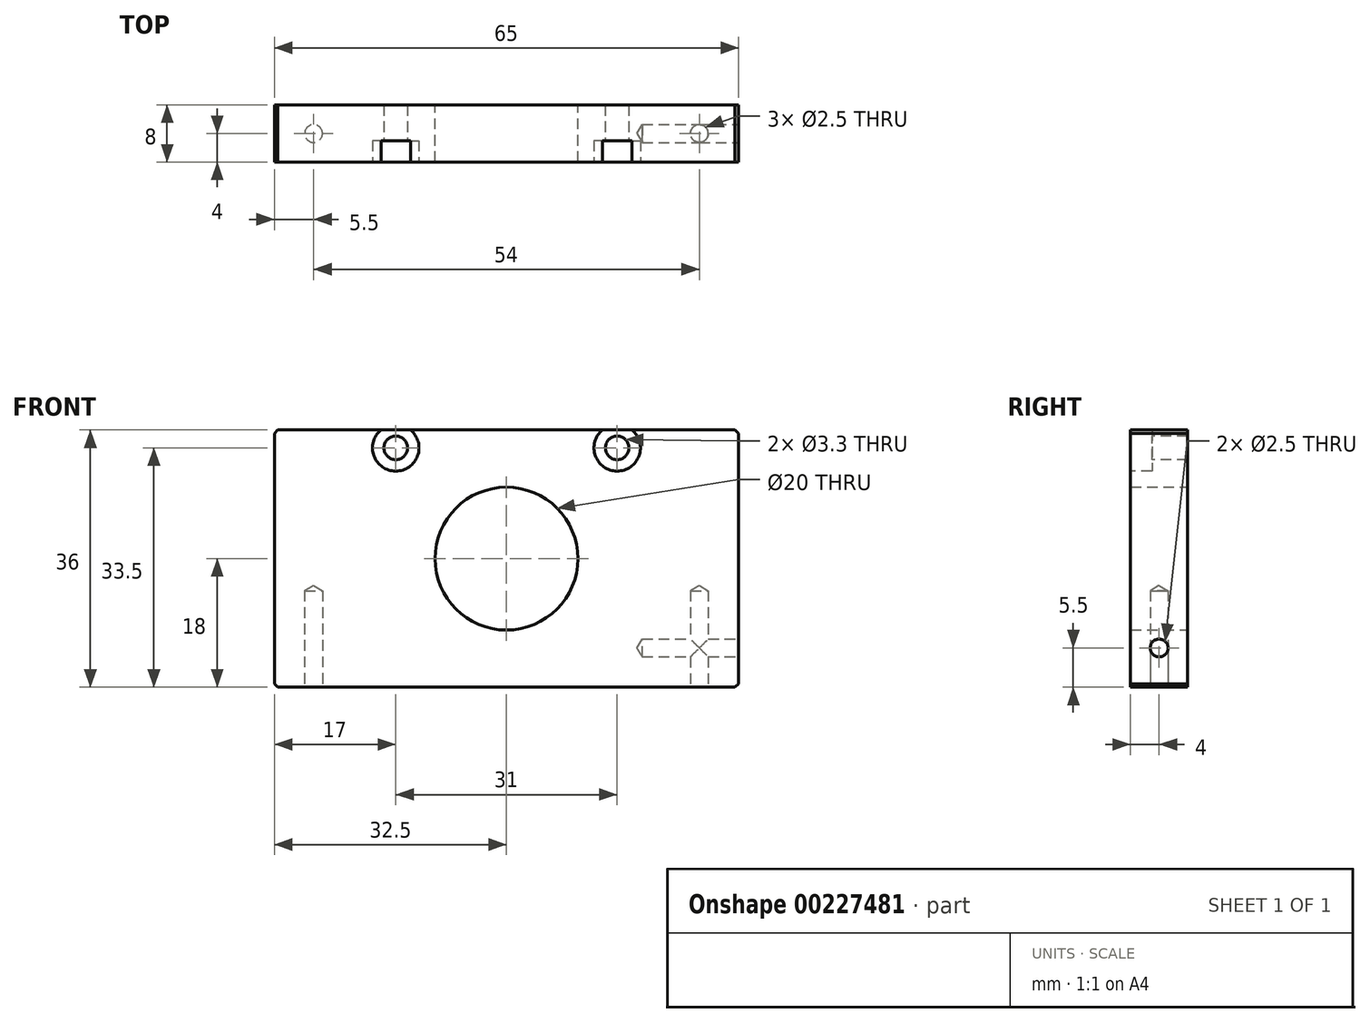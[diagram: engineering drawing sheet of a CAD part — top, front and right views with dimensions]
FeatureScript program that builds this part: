
annotation { "Feature Type Name" : "Feature", "Feature Type Description" : "" }
export const myFeature = defineFeature(function(context is Context, id is Id, definition is map)
    precondition{}
    {
        {
            var Q0;
            Q0=qCreatedBy(makeId("Front.planeOp"),FACE);
            var sketch = newSketch(context, id + "F0", { "sketchPlane" : qUnion([Q0])});
            skLineSegment(sketch, "E0.bottom", {"start": v(32.5, -18) * mm, "end": v(-32.5, -18) * mm});
            skLineSegment(sketch, "E0.top", {"start": v(32.5, 18) * mm, "end": v(-32.5, 18) * mm});
            skLineSegment(sketch, "E0.left", {"start": v(32.5, -18) * mm, "end": v(32.5, 18) * mm});
            skLineSegment(sketch, "E0.right", {"start": v(-32.5, -18) * mm, "end": v(-32.5, 18) * mm});
            skPoint(sketch, "E0.middle", {"position": v(0, 0) * mm});
            skCircle(sketch, "E1", {"center": v(0, 0) * mm, "radius": 10 * mm});
            skSolve(sketch);
        }
        {
            var Q0;
            Q0=makeQuery(id+"F0.imprint","IMPRINT",FACE,{"disambiguationData":[TD([[makeQuery(id+"F0.imprint","IMPRINT",EDGE,{"derivedFrom":sQuery(id+"F0.wireOp",EDGE,"E0.bottom")}),-1.0]])]});
            extrude(context, id + "F1", {"entities" : qUnion([Q0]), "depth" : 8 * mm});
        }
        {
            var Q0;
            Q0=makeQuery(id+"F1.opExtrude","CAP_FACE",FACE,{"disambiguationData":[OSD([sQuery(id+"F0.wireOp",EDGE,"E0.bottom"),sQuery(id+"F0.wireOp",EDGE,"E0.top"),sQuery(id+"F0.wireOp",EDGE,"E0.left"),sQuery(id+"F0.wireOp",EDGE,"E0.right")])],"isStart":false});
            var sketch = newSketch(context, id + "F2", { "sketchPlane" : qUnion([Q0])});
            skPoint(sketch, "E2", {"position": v(15.5, 15.5) * mm});
            skPoint(sketch, "E3.MirrorP", {"position": v(-15.5, 15.5) * mm});
            skPoint(sketch, "E4.MirrorP", {"position": v(15.5, -15.5) * mm});
            skPoint(sketch, "E5.MirrorP", {"position": v(-15.5, -15.5) * mm});
            skSolve(sketch);
        }
        {
            var Q0;
            Q0=sQuery(id+"F2.wireOp",VERTEX,"E2");
            var Q1;
            Q1=sQuery(id+"F2.wireOp",VERTEX,"E3.MirrorP");
            var Q2;
            Q2=makeQuery(id+"F1.opExtrude","SWEPT_BODY",BODY,{"disambiguationData":[OSD([sQuery(id+"F0.wireOp",EDGE,"E0.bottom"),sQuery(id+"F0.wireOp",EDGE,"E0.top"),sQuery(id+"F0.wireOp",EDGE,"E0.left"),sQuery(id+"F0.wireOp",EDGE,"E0.right")])]});
            hole(context, id + "F3", {"style" : HoleStyle.C_BORE, "endStyle" : HoleEndStyle.THROUGH, "standardTappedOrClearance" : lookupTablePath({ "standard" : "ISO", "fit" : "Normal", "size" : "M3", "type" : "Clearance" }), "standardBlindInLast" : lookupTablePath({ "fit" : "Standard", "standard" : "ISO", "size" : "M3", "type" : "Clearance" }), "holeDiameter" : 3.3 * mm, "cBoreDiameter" : 6.5 * mm, "cBoreDepth" : 3 * mm, "locations" : qUnion([Q0, Q1]), "scope" : qUnion([Q2]), "tappedDepth" : 12 * mm, "tapClearance" : 3});
        }
        {
            var Q0;
            Q0=makeQuery(id+"F1.opExtrude","SWEPT_EDGE",EDGE,{"disambiguationData":[OSD([sQuery(id+"F0.wireOp",EDGE,"E0.top"),sQuery(id+"F0.wireOp",EDGE,"E0.right")])]});
            var Q1;
            Q1=makeQuery(id+"F1.opExtrude","SWEPT_EDGE",EDGE,{"disambiguationData":[OSD([sQuery(id+"F0.wireOp",EDGE,"E0.top"),sQuery(id+"F0.wireOp",EDGE,"E0.left")])]});
            var Q2;
            Q2=makeQuery(id+"F1.opExtrude","SWEPT_EDGE",EDGE,{"disambiguationData":[OSD([sQuery(id+"F0.wireOp",EDGE,"E0.bottom"),sQuery(id+"F0.wireOp",EDGE,"E0.left")])]});
            var Q3;
            Q3=makeQuery(id+"F1.opExtrude","SWEPT_EDGE",EDGE,{"disambiguationData":[OSD([sQuery(id+"F0.wireOp",EDGE,"E0.bottom"),sQuery(id+"F0.wireOp",EDGE,"E0.right")])]});
            chamfer(context, id + "F4", {"entities" : qUnion([Q0, Q1, Q2, Q3]), "width" : 0.5 * mm, "tangentPropagation" : true});
        }
        {
            var Q0;
            Q0=makeQuery(id+"F1.opExtrude","SWEPT_FACE",FACE,{"disambiguationData":[OSD([sQuery(id+"F0.wireOp",EDGE,"E0.bottom")])]});
            var sketch = newSketch(context, id + "F5", { "sketchPlane" : qUnion([Q0])});
            skPoint(sketch, "E6", {"position": v(27, 4) * mm});
            skPoint(sketch, "E7.MirrorP", {"position": v(-27, 4) * mm});
            skSolve(sketch);
        }
        {
            var Q0;
            Q0=sQuery(id+"F5.wireOp",VERTEX,"E6");
            var Q1;
            Q1=sQuery(id+"F5.wireOp",VERTEX,"E7.MirrorP");
            var Q2;
            Q2=makeQuery(id+"F1.opExtrude","SWEPT_BODY",BODY,{"disambiguationData":[OSD([sQuery(id+"F0.wireOp",EDGE,"E0.bottom"),sQuery(id+"F0.wireOp",EDGE,"E0.top"),sQuery(id+"F0.wireOp",EDGE,"E0.left"),sQuery(id+"F0.wireOp",EDGE,"E0.right"),sQuery(id+"F0.wireOp",EDGE,"E1")])]});
            hole(context, id + "F6", {"style" : HoleStyle.SIMPLE, "endStyle" : HoleEndStyle.BLIND, "standardTappedOrClearance" : lookupTablePath({ "standard" : "ISO", "engagement" : "75%", "pitch" : "0.5 mm", "size" : "M3", "type" : "Tapped" }), "standardBlindInLast" : lookupTablePath({ "standard" : "ISO", "engagement" : "75%", "pitch" : "0.5 mm", "size" : "M3", "type" : "Tapped" }), "holeDiameter" : 2.5 * mm, "holeDepth" : 13.5 * mm, "locations" : qUnion([Q0, Q1]), "scope" : qUnion([Q2]), "showTappedDepth" : true, "tappedDepth" : 12 * mm, "tapClearance" : 3, "majorDiameter" : 3 * mm});
        }
        {
            var Q0;
            Q0=makeQuery(id+"F1.opExtrude","SWEPT_FACE",FACE,{"disambiguationData":[OSD([sQuery(id+"F0.wireOp",EDGE,"E0.left")])]});
            var sketch = newSketch(context, id + "F7", { "sketchPlane" : qUnion([Q0])});
            skPoint(sketch, "E8", {"position": v(-4, -12.5) * mm});
            skPoint(sketch, "E8.positionSnap0", {"position": v(-4, -17.5) * mm});
            skSolve(sketch);
        }
        {
            var Q0;
            Q0=sQuery(id+"F7.wireOp",VERTEX,"E8");
            var Q1;
            Q1=makeQuery(id+"F1.opExtrude","SWEPT_BODY",BODY,{"disambiguationData":[OSD([sQuery(id+"F0.wireOp",EDGE,"E0.bottom"),sQuery(id+"F0.wireOp",EDGE,"E0.top"),sQuery(id+"F0.wireOp",EDGE,"E0.left"),sQuery(id+"F0.wireOp",EDGE,"E0.right"),sQuery(id+"F0.wireOp",EDGE,"E1")])]});
            hole(context, id + "F8", {"style" : HoleStyle.SIMPLE, "endStyle" : HoleEndStyle.BLIND, "standardTappedOrClearance" : lookupTablePath({ "standard" : "ISO", "engagement" : "75%", "pitch" : "0.5 mm", "size" : "M3", "type" : "Tapped" }), "standardBlindInLast" : lookupTablePath({ "standard" : "ISO", "engagement" : "75%", "pitch" : "0.5 mm", "size" : "M3", "type" : "Tapped" }), "holeDiameter" : 2.5 * mm, "showTappedDepth" : true, "holeDepth" : 13.5 * mm, "tappedDepth" : 12 * mm, "tapClearance" : 3, "locations" : qUnion([Q0]), "scope" : qUnion([Q1]), "majorDiameter" : 3 * mm});
        }
    });
